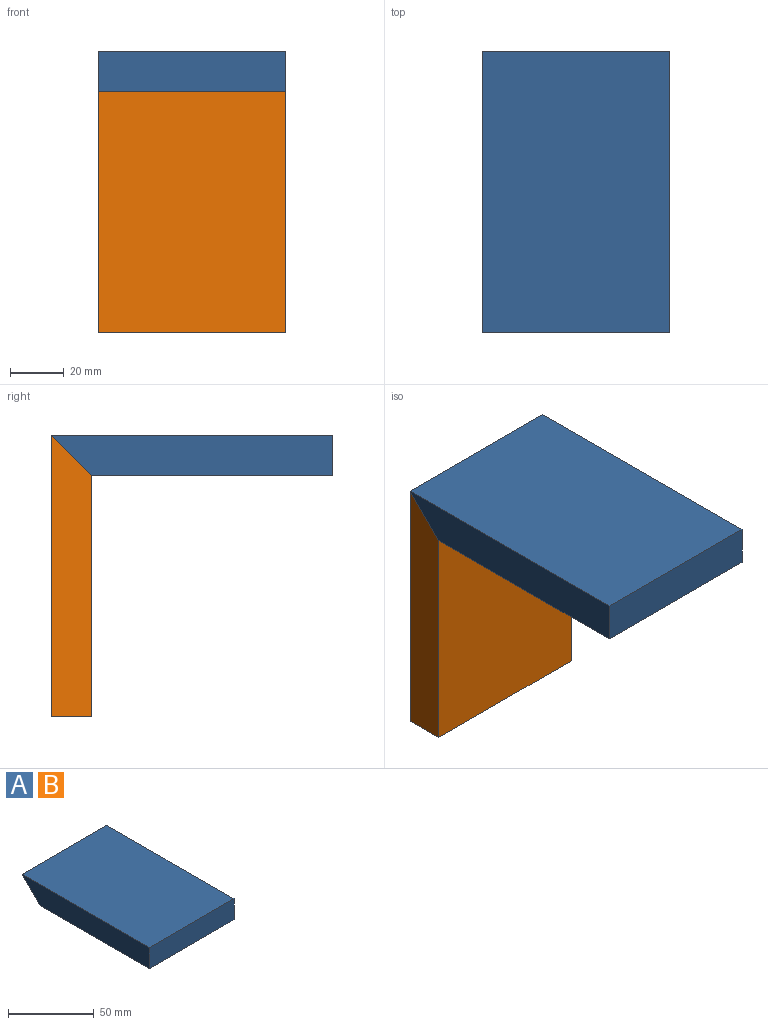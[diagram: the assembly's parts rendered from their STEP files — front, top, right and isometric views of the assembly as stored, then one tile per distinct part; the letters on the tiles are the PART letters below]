
ASSEMBLY  parts=2 mates=1
PART A: 6 faces, bbox 70x105x15 mm
  f0: plane 105x70mm, normal (0,0,1), area 7350mm2, adj f1,f3,f4,f5
  f1: plane 70x15mm, normal (0,-1,0), area 1050mm2, adj f0,f2,f4,f5
  f2: plane 90x70mm, normal (0,0,-1), area 6300mm2, adj f1,f3,f4,f5
  f3: plane 70x15mm, normal (0,0.71,-0.71), area 1484.9mm2, adj f0,f2,f4,f5
  f4: plane 105x15mm, normal (1,0,0), area 1462.5mm2, adj f0,f1,f2,f3
  f5: plane 105x15mm, normal (-1,0,0), area 1462.5mm2, adj f0,f1,f2,f3
PART B: same geometry as A
PLACE A t=(-43.22,25.36,-26.08)mm
PLACE B rot(axis=(0,0.71,0.71),180deg) t=(26.78,25.36,-26.08)mm
MATE planar B.f3 <-> A.f3  axis (0,-0.71,0.71) through (-8.22,17.86,-33.58)mm
